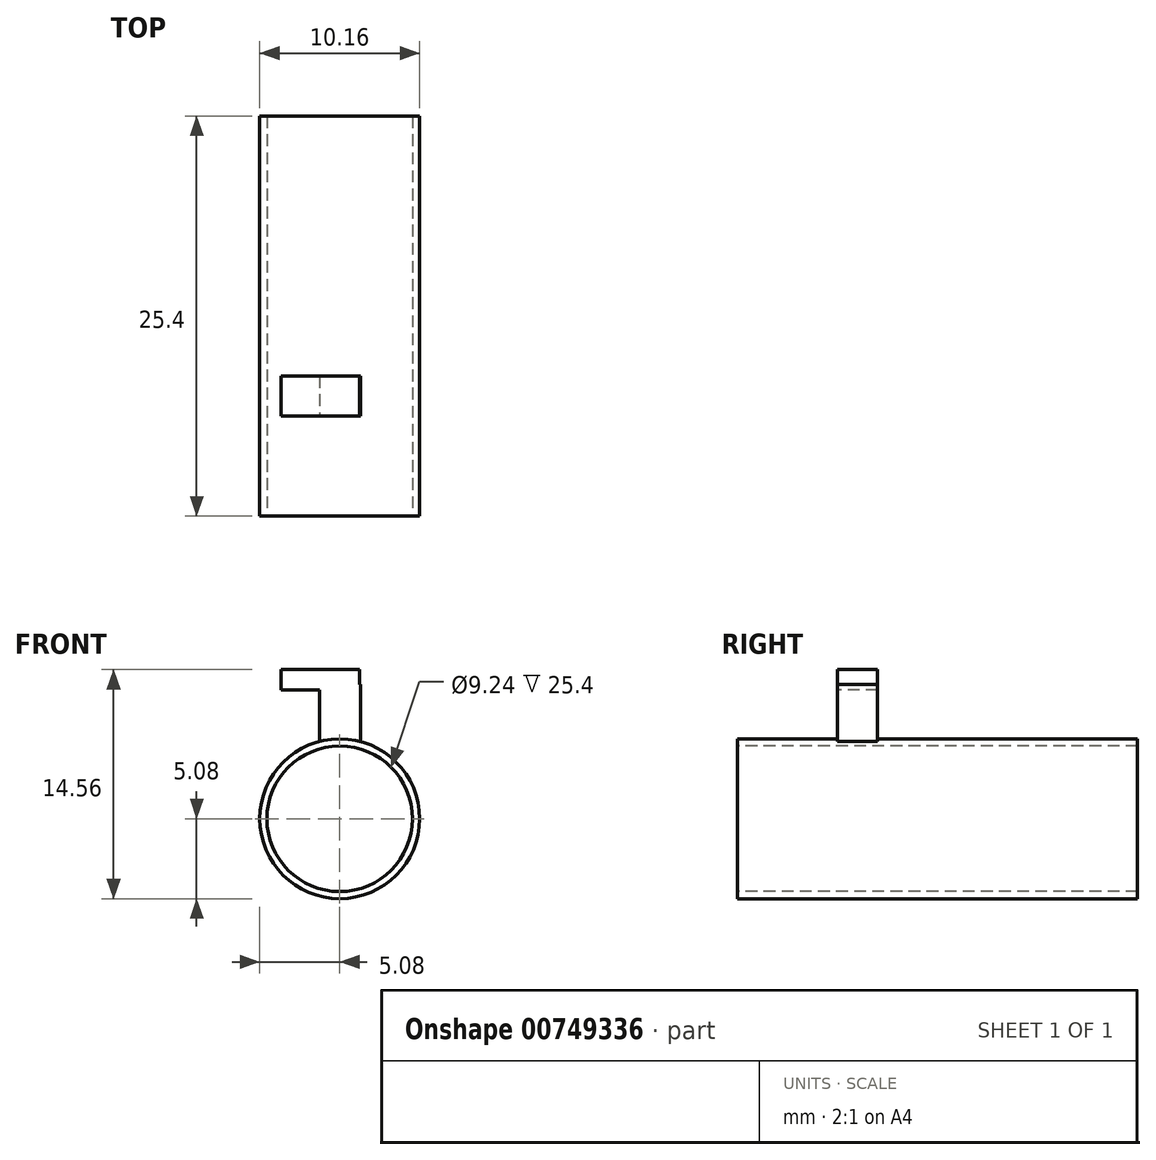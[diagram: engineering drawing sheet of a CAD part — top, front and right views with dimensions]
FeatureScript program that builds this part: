
annotation { "Feature Type Name" : "Feature", "Feature Type Description" : "" }
export const myFeature = defineFeature(function(context is Context, id is Id, definition is map)
    precondition{}
    {
        {
            var Q0;
            Q0=qCreatedBy(makeId("Front.planeOp"),FACE);
            var sketch = newSketch(context, id + "F0", { "sketchPlane" : qUnion([Q0])});
            skCircle(sketch, "E0", {"center": v(0, 0) * mm, "radius": 5.08 * mm});
            skSolve(sketch);
        }
        {
            var Q0;
            Q0 = qSketchRegion(id + "F0", true);
            extrude(context, id + "F1", {"entities" : qUnion([Q0]), "depth" : 25.4 * mm, "offsetDistance" : 25.4 * mm});
        }
        {
            var Q0;
            Q0=makeQuery(id+"F1.opExtrude","CAP_FACE",FACE,{"disambiguationData":[OSD([sQuery(id+"F0.wireOp",EDGE,"E0")])],"isStart":false});
            var sketch = newSketch(context, id + "F2", { "sketchPlane" : qUnion([Q0])});
            skCircle(sketch, "E1", {"center": v(0, 0) * mm, "radius": 4.62 * mm});
            skSolve(sketch);
        }
        {
            var Q0;
            Q0 = qSketchRegion(id + "F2", true);
            extrude(context, id + "F3", {"entities" : qUnion([Q0]), "operationType" : NewBodyOperationType.REMOVE, "oppositeDirection" : true, "depth" : 25.4 * mm, "offsetDistance" : 25.4 * mm});
        }
        {
            var Q0;
            Q0=qCreatedBy(makeId("Front.planeOp"),FACE);
            cPlane(context, id + "F4", {"entities" : qUnion([Q0]), "cplaneType" : CPlaneType.OFFSET, "offset" : 19.05 * mm, "width" : 152.4 * mm, "height" : 152.4 * mm});
        }
        {
            var Q0;
            Q0=qCreatedBy(id+"F4.planeOp",FACE);
            var sketch = newSketch(context, id + "F5", { "sketchPlane" : qUnion([Q0])});
            skLineSegment(sketch, "E2.bottom", {"start": v(-1.29, 4.87) * mm, "end": v(1.32, 4.87) * mm});
            skLineSegment(sketch, "E2.top", {"start": v(-1.29, 8.53) * mm, "end": v(1.32, 8.53) * mm});
            skLineSegment(sketch, "E2.left", {"start": v(-1.29, 4.87) * mm, "end": v(-1.29, 8.53) * mm});
            skLineSegment(sketch, "E2.right", {"start": v(1.32, 4.87) * mm, "end": v(1.32, 8.53) * mm});
            skSolve(sketch);
        }
        {
            var Q0;
            Q0 = qSketchRegion(id + "F5", true);
            extrude(context, id + "F6", {"entities" : qUnion([Q0]), "operationType" : NewBodyOperationType.ADD, "oppositeDirection" : true, "depth" : 2.54 * mm, "offsetDistance" : 25.4 * mm});
        }
        {
            var Q0;
            Q0=qCreatedBy(id+"F4.planeOp",FACE);
            var sketch = newSketch(context, id + "F7", { "sketchPlane" : qUnion([Q0])});
            skLineSegment(sketch, "E3.bottom", {"start": v(1.28, 8.19) * mm, "end": v(-3.74, 8.19) * mm});
            skLineSegment(sketch, "E3.top", {"start": v(1.28, 9.48) * mm, "end": v(-3.74, 9.48) * mm});
            skLineSegment(sketch, "E3.left", {"start": v(1.28, 8.19) * mm, "end": v(1.28, 9.48) * mm});
            skLineSegment(sketch, "E3.right", {"start": v(-3.74, 8.19) * mm, "end": v(-3.74, 9.48) * mm});
            skSolve(sketch);
        }
        {
            var Q0;
            Q0 = qSketchRegion(id + "F7", true);
            extrude(context, id + "F8", {"entities" : qUnion([Q0]), "operationType" : NewBodyOperationType.ADD, "oppositeDirection" : true, "depth" : 2.54 * mm, "offsetDistance" : 25.4 * mm});
        }
    });
